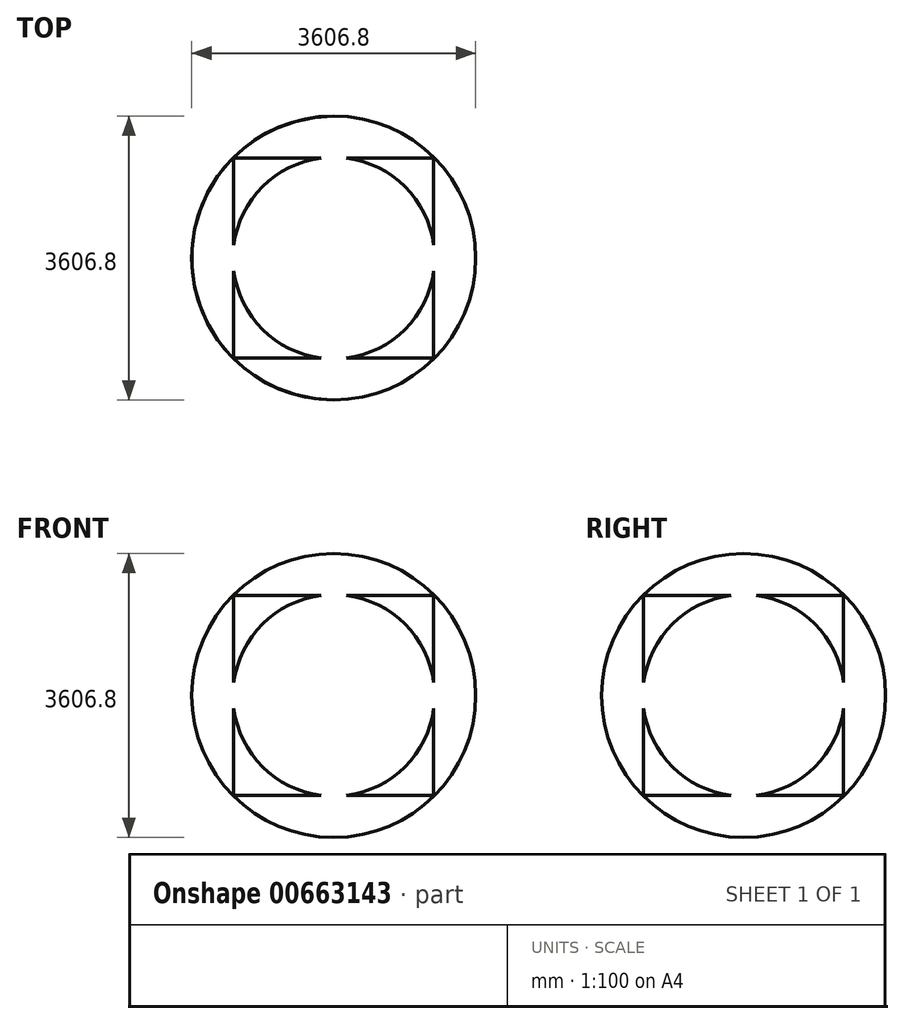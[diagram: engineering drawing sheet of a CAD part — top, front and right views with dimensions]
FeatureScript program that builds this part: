
annotation { "Feature Type Name" : "Feature", "Feature Type Description" : "" }
export const myFeature = defineFeature(function(context is Context, id is Id, definition is map)
    precondition{}
    {
        {
            var Q0;
            Q0=qCreatedBy(makeId("Top.planeOp"),FACE);
            cPlane(context, id + "F0", {"entities" : qUnion([Q0]), "cplaneType" : CPlaneType.OFFSET, "offset" : 1270 * mm, "width" : 152.4 * mm, "height" : 152.4 * mm});
        }
        {
            var Q0;
            Q0=qCreatedBy(makeId("Top.planeOp"),FACE);
            var sketch = newSketch(context, id + "F1", { "sketchPlane" : qUnion([Q0])});
            skLineSegment(sketch, "E0.bottom", {"start": v(1270, -1270) * mm, "end": v(-1270, -1270) * mm});
            skLineSegment(sketch, "E0.top", {"start": v(1270, 1270) * mm, "end": v(-1270, 1270) * mm});
            skLineSegment(sketch, "E0.left", {"start": v(1270, -1270) * mm, "end": v(1270, 1270) * mm});
            skLineSegment(sketch, "E0.right", {"start": v(-1270, -1270) * mm, "end": v(-1270, 1270) * mm});
            skPoint(sketch, "E0.middle", {"position": v(0, 0) * mm});
            skSolve(sketch);
        }
        {
            var Q0;
            Q0=qCreatedBy(id+"F0.planeOp",FACE);
            var sketch = newSketch(context, id + "F2", { "sketchPlane" : qUnion([Q0])});
            skPoint(sketch, "E1.start.orphan", {"position": v(0, 1277.57) * mm});
            skArc(sketch, "E2", {"start": v(0, 1803.4) * mm, "mid": v(-1803.4, 0) * mm, "end": v(0, -1803.4) * mm});
            skLineSegment(sketch, "E3", {"start": v(0, 1803.4) * mm, "end": v(0, -1803.4) * mm});
            skSolve(sketch);
        }
        {
            var Q0;
            Q0 = qSketchRegion(id + "F1", true);
            extrude(context, id + "F3", {"entities" : qUnion([Q0]), "depth" : 2540 * mm, "offsetDistance" : 25.4 * mm});
        }
        {
            var Q0;
            Q0 = qSketchRegion(id + "F2", true);
            var Q1;
            Q1=sQuery(id+"F2.wireOp",EDGE,"E3");
            revolve(context, id + "F4", {"operationType" : NewBodyOperationType.ADD, "entities" : qUnion([Q0]), "axis" : qUnion([Q1]), "revolveType" : RevolveType.FULL});
        }
    });
